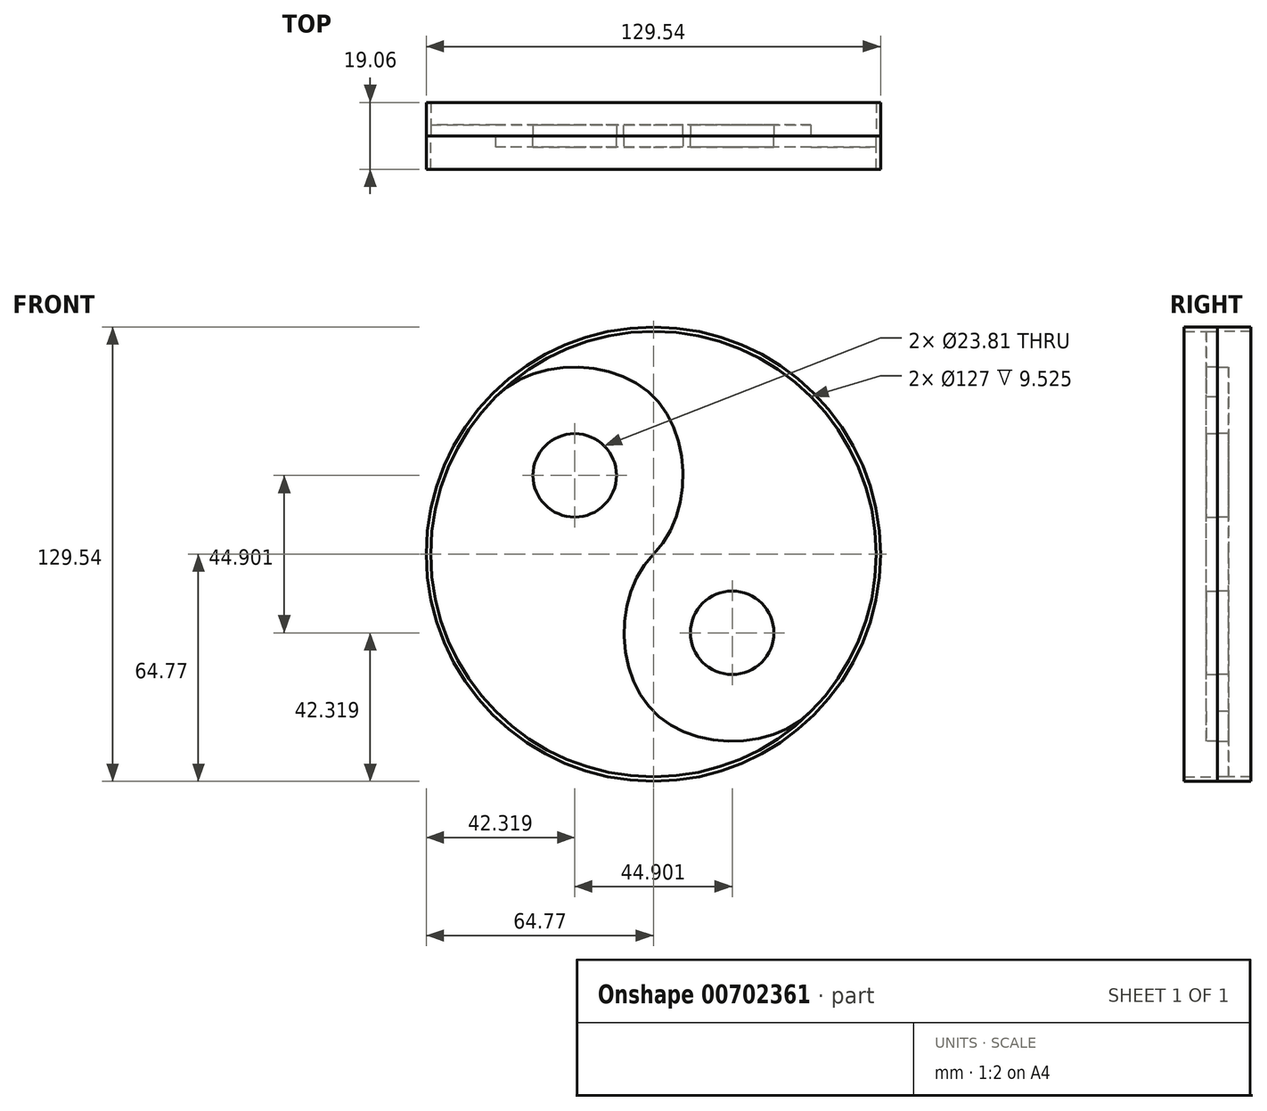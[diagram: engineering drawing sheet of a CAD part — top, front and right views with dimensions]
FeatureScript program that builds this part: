
annotation { "Feature Type Name" : "Feature", "Feature Type Description" : "" }
export const myFeature = defineFeature(function(context is Context, id is Id, definition is map)
    precondition{}
    {
        {
            var Q0;
            Q0=qCreatedBy(makeId("Front.planeOp"),FACE);
            var sketch = newSketch(context, id + "F0", { "sketchPlane" : qUnion([Q0])});
            skCircle(sketch, "E0", {"center": v(0, 0) * mm, "radius": 63.5 * mm});
            skLineSegment(sketch, "E1", {"start": v(0, 0) * mm, "end": v(0, 63.5) * mm, "construction": true});
            skLineSegment(sketch, "E2", {"start": v(0, 63.5) * mm, "end": v(-63.5, 0) * mm, "construction": true});
            skLineSegment(sketch, "E3", {"start": v(0, -63.5) * mm, "end": v(63.5, 0) * mm, "construction": true});
            skLineSegment(sketch, "E4", {"start": v(63.5, 0) * mm, "end": v(0, 0) * mm, "construction": true});
            skLineSegment(sketch, "E5", {"start": v(-44.9, 0) * mm, "end": v(0, 44.9) * mm, "construction": true});
            skFitSpline(sketch, "E6", {"points": [v(-44.9, 44.9) * mm, v(-44.9, 0) * mm, v(0, 0) * mm, v(0, 44.9) * mm, v(-44.9, 44.9) * mm]});
            skLineSegment(sketch, "E7", {"start": v(0, -44.9) * mm, "end": v(44.9, 0) * mm, "construction": true});
            skFitSpline(sketch, "E8", {"points": [v(0, 0) * mm, v(44.9, 0) * mm, v(44.9, -44.9) * mm, v(0, -44.9) * mm, v(0, 0) * mm]});
            skLineSegment(sketch, "E9", {"start": v(-44.9, 0) * mm, "end": v(0, -63.5) * mm, "construction": true});
            skLineSegment(sketch, "E10", {"start": v(-44.9, 44.9) * mm, "end": v(-22.45, 22.45) * mm});
            skLineSegment(sketch, "E11", {"start": v(-22.45, 22.45) * mm, "end": v(0, 0) * mm});
            skLineSegment(sketch, "E12", {"start": v(0, 0) * mm, "end": v(22.45, -22.45) * mm, "construction": true});
            skLineSegment(sketch, "E13", {"start": v(22.45, -22.45) * mm, "end": v(44.9, -44.9) * mm, "construction": true});
            skLineSegment(sketch, "E14", {"start": v(0, -44.9) * mm, "end": v(44.9, -44.9) * mm, "construction": true});
            skCircle(sketch, "E15", {"center": v(-22.45, 22.45) * mm, "radius": 11.9 * mm});
            skCircle(sketch, "E16", {"center": v(22.45, -22.45) * mm, "radius": 11.9 * mm});
            skSolve(sketch);
        }
        {
            var Q0;
            {var subQ1=sQuery(id+"F0.wireOp",EDGE,"E0");var subQ3=sQuery(id+"F0.wireOp",EDGE,"E8");var subQ4=makeQuery(id+"F0.imprint","INTERSECT",VERTEX,{"derivedFrom":[subQ1,subQ3]});Q0=makeQuery(id+"F0.imprint","IMPRINT",FACE,{"disambiguationData":[TD([[makeQuery(id+"F0.imprint","IMPRINT",EDGE,{"disambiguationData":[TD([[subQ4,-1.0]])],"derivedFrom":subQ3}),1.0]])]});}
            var Q1;
            {var subQ4=sQuery(id+"F0.wireOp",EDGE,"E15");var subQ6=sQuery(id+"F0.wireOp",EDGE,"E10");var subQ8=makeQuery(id+"F0.imprint","INTERSECT",VERTEX,{"derivedFrom":[subQ6,subQ4]});Q1=makeQuery(id+"F0.imprint","IMPRINT",FACE,{"disambiguationData":[TD([[makeQuery(id+"F0.imprint","IMPRINT",EDGE,{"disambiguationData":[TD([[subQ8,-1.0]])],"derivedFrom":subQ4}),-1.0]])]});}
            var Q2;
            {var subQ0=sQuery(id+"F0.wireOp",EDGE,"E10");var subQ5=sQuery(id+"F0.wireOp",EDGE,"E15");var subQ6=makeQuery(id+"F0.imprint","INTERSECT",VERTEX,{"derivedFrom":[subQ0,subQ5]});Q2=makeQuery(id+"F0.imprint","IMPRINT",FACE,{"disambiguationData":[TD([[makeQuery(id+"F0.imprint","IMPRINT",EDGE,{"disambiguationData":[TD([[subQ6,1.0]])],"derivedFrom":subQ5}),-1.0]])]});}
            var Q3;
            Q3=makeQuery(id+"F0.imprint","IMPRINT",FACE,{"disambiguationData":[TD([[makeQuery(id+"F0.imprint","IMPRINT",EDGE,{"derivedFrom":sQuery(id+"F0.wireOp",EDGE,"E16")}),1.0]])]});
            extrude(context, id + "F1", {"entities" : qUnion([Q0, Q1, Q2, Q3]), "oppositeDirection" : true, "depth" : 3.17 * mm});
        }
        {
            var Q0;
            Q0=qCreatedBy(makeId("Front.planeOp"),FACE);
            var sketch = newSketch(context, id + "F2", { "sketchPlane" : qUnion([Q0])});
            skCircle(sketch, "E17", {"center": v(0, 0) * mm, "radius": 63.5 * mm});
            skCircle(sketch, "E18", {"center": v(0, 0) * mm, "radius": 64.77 * mm});
            skSolve(sketch);
        }
        {
            var Q0;
            Q0=qSketchRegion(id+"F2",true);
            extrude(context, id + "F3", {"entities" : qUnion([Q0]), "operationType" : NewBodyOperationType.ADD, "depth" : 9.52 * mm});
        }
        {
            var Q0;
            {var subQ1=sQuery(id+"F0.wireOp",EDGE,"E0");var subQ3=sQuery(id+"F0.wireOp",EDGE,"E8");var subQ4=makeQuery(id+"F0.imprint","INTERSECT",VERTEX,{"derivedFrom":[subQ1,subQ3]});Q0=makeQuery(id+"F0.imprint","IMPRINT",FACE,{"disambiguationData":[TD([[makeQuery(id+"F0.imprint","IMPRINT",EDGE,{"disambiguationData":[TD([[subQ4,-1.0]])],"derivedFrom":subQ1}),1.0]])]});}
            var Q1;
            Q1=makeQuery(id+"F0.imprint","IMPRINT",FACE,{"disambiguationData":[TD([[makeQuery(id+"F0.imprint","IMPRINT",EDGE,{"derivedFrom":sQuery(id+"F0.wireOp",EDGE,"E16")}),-1.0]])]});
            var Q2;
            {var subQ0=sQuery(id+"F0.wireOp",EDGE,"E11");var subQ1=sQuery(id+"F0.wireOp",EDGE,"E10");var subQ2=makeQuery(id+"F0.imprint","INTERSECT",VERTEX,{"derivedFrom":[subQ1,subQ0]});Q2=makeQuery(id+"F0.imprint","IMPRINT",FACE,{"disambiguationData":[TD([[makeQuery(id+"F0.imprint","IMPRINT",EDGE,{"disambiguationData":[TD([[subQ2,1.0]])],"derivedFrom":subQ1}),-1.0]])]});}
            var Q3;
            {var subQ0=sQuery(id+"F0.wireOp",EDGE,"E11");var subQ1=sQuery(id+"F0.wireOp",EDGE,"E10");var subQ2=makeQuery(id+"F0.imprint","INTERSECT",VERTEX,{"derivedFrom":[subQ1,subQ0]});Q3=makeQuery(id+"F0.imprint","IMPRINT",FACE,{"disambiguationData":[TD([[makeQuery(id+"F0.imprint","IMPRINT",EDGE,{"disambiguationData":[TD([[subQ2,1.0]])],"derivedFrom":subQ1}),1.0]])]});}
            extrude(context, id + "F4", {"entities" : qUnion([Q0, Q1, Q2, Q3]), "depth" : 3.17 * mm});
        }
        {
            var Q0;
            Q0=qSketchRegion(id+"F2",true);
            extrude(context, id + "F5", {"entities" : qUnion([Q0]), "oppositeDirection" : true, "depth" : 9.52 * mm});
        }
    });
